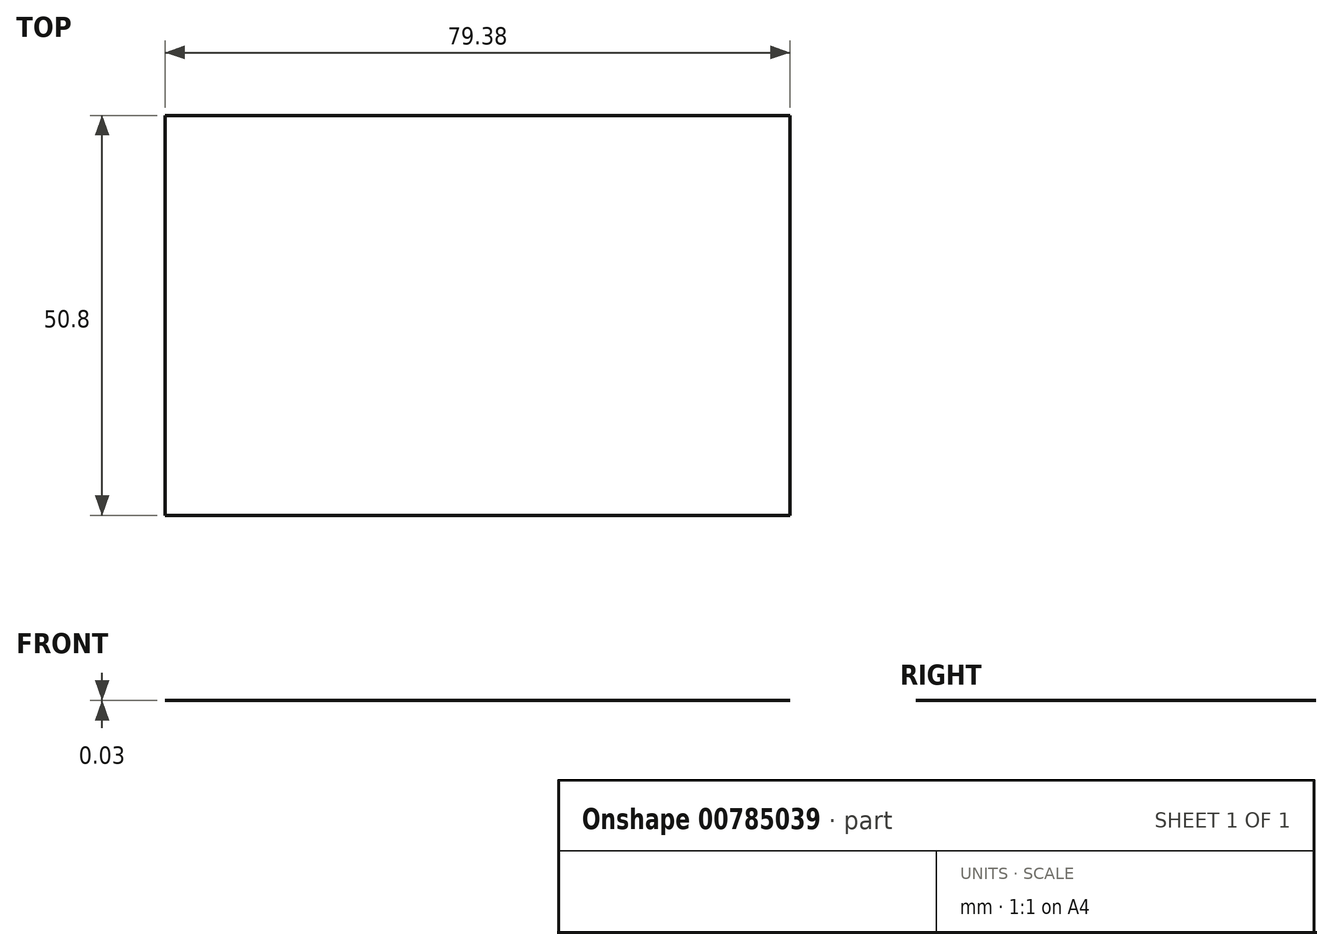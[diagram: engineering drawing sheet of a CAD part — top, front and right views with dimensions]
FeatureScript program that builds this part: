
annotation { "Feature Type Name" : "Feature", "Feature Type Description" : "" }
export const myFeature = defineFeature(function(context is Context, id is Id, definition is map)
    precondition{}
    {
        {
            var Q0;
            Q0=qCreatedBy(makeId("Top.planeOp"),FACE);
            var sketch = newSketch(context, id + "F0", { "sketchPlane" : qUnion([Q0])});
            skLineSegment(sketch, "E0.bottom", {"start": v(0, 0) * mm, "end": v(79.38, 0) * mm});
            skLineSegment(sketch, "E0.top", {"start": v(0, 50.8) * mm, "end": v(79.37, 50.8) * mm});
            skLineSegment(sketch, "E0.left", {"start": v(0, 0) * mm, "end": v(0, 50.8) * mm});
            skLineSegment(sketch, "E0.right", {"start": v(79.38, 0) * mm, "end": v(79.37, 50.8) * mm});
            skSolve(sketch);
        }
        {
            var Q0;
            Q0 = qSketchRegion(id + "F0", true);
            extrude(context, id + "F1", {"entities" : qUnion([Q0]), "depth" : 3 / 101.6 * mm, "offsetDistance" : 25.4 * mm});
        }
    });
